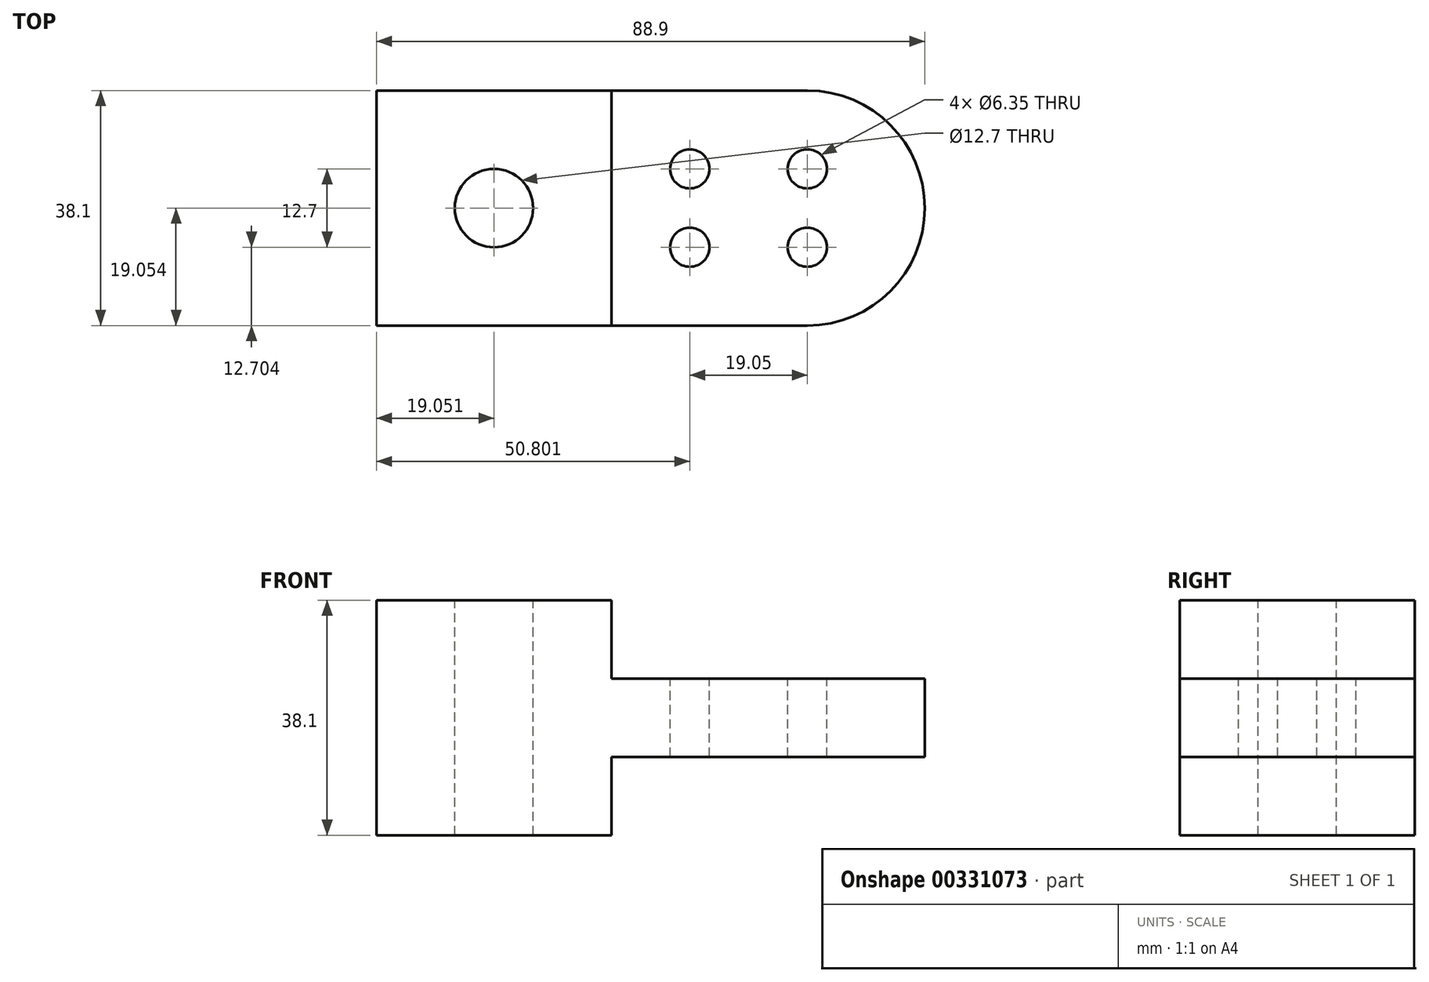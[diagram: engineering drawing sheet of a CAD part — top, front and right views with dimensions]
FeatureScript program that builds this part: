
annotation { "Feature Type Name" : "Feature", "Feature Type Description" : "" }
export const myFeature = defineFeature(function(context is Context, id is Id, definition is map)
    precondition{}
    {
        {
            var Q0;
            Q0=qCreatedBy(makeId("Top.planeOp"),FACE);
            var sketch = newSketch(context, id + "F0", { "sketchPlane" : qUnion([Q0])});
            skLineSegment(sketch, "E0", {"start": v(-35.89, 29.52) * mm, "end": v(2.21, 29.52) * mm});
            skLineSegment(sketch, "E1", {"start": v(2.21, 29.52) * mm, "end": v(2.21, -8.58) * mm});
            skLineSegment(sketch, "E2", {"start": v(2.21, -8.58) * mm, "end": v(-35.89, -8.58) * mm});
            skLineSegment(sketch, "E3", {"start": v(-35.89, -8.58) * mm, "end": v(-35.89, 29.52) * mm});
            skSolve(sketch);
        }
        {
            var Q0;
            Q0 = qSketchRegion(id + "F0", true);
            extrude(context, id + "F1", {"entities" : qUnion([Q0]), "depth" : 38.1 * mm});
        }
        {
            var Q0;
            Q0=makeQuery(id+"F1.opExtrude","SWEPT_FACE",FACE,{"disambiguationData":[OSD([sQuery(id+"F0.wireOp",EDGE,"E2")])]});
            var sketch = newSketch(context, id + "F2", { "sketchPlane" : qUnion([Q0])});
            skLineSegment(sketch, "E4", {"start": v(2.21, 19.05) * mm, "end": v(2.21, 25.4) * mm});
            skLineSegment(sketch, "E5", {"start": v(2.21, 25.4) * mm, "end": v(33.96, 25.4) * mm});
            skLineSegment(sketch, "E6", {"start": v(33.96, 25.4) * mm, "end": v(33.96, 12.7) * mm});
            skLineSegment(sketch, "E7", {"start": v(33.96, 12.7) * mm, "end": v(2.21, 12.7) * mm});
            skLineSegment(sketch, "E8", {"start": v(2.21, 12.7) * mm, "end": v(2.21, 19.05) * mm});
            skSolve(sketch);
        }
        {
            var Q0;
            Q0 = qSketchRegion(id + "F2", true);
            extrude(context, id + "F3", {"entities" : qUnion([Q0]), "operationType" : NewBodyOperationType.ADD, "oppositeDirection" : true, "depth" : 38.1 * mm});
        }
        {
            var Q0;
            Q0=makeQuery(id+"F3.opExtrude","SWEPT_FACE",FACE,{"disambiguationData":[OSD([sQuery(id+"F2.wireOp",EDGE,"E5")])]});
            var sketch = newSketch(context, id + "F4", { "sketchPlane" : qUnion([Q0])});
            skArc(sketch, "E9", {"start": v(33.96, -8.58) * mm, "mid": v(53.01, 10.47) * mm, "end": v(33.96, 29.52) * mm});
            skSolve(sketch);
        }
        {
            var Q0;
            Q0 = qSketchRegion(id + "F4", true);
            var Q1;
            Q1=makeQuery(id+"F4.imprint","IMPRINT",FACE,{"disambiguationData":[TD([[makeQuery(id+"F4.imprint","IMPRINT",EDGE,{"derivedFrom":sQuery(id+"F4.wireOp",EDGE,"E9")}),1.0]])]});
            extrude(context, id + "F5", {"entities" : qUnion([Q0, Q1]), "operationType" : NewBodyOperationType.ADD, "oppositeDirection" : true, "depth" : 12.7 * mm});
        }
        {
            var Q0;
            Q0=makeQuery(id+"F1.opExtrude","CAP_FACE",FACE,{"disambiguationData":[OSD([sQuery(id+"F0.wireOp",EDGE,"E0"),sQuery(id+"F0.wireOp",EDGE,"E1"),sQuery(id+"F0.wireOp",EDGE,"E2"),sQuery(id+"F0.wireOp",EDGE,"E3")])],"isStart":false});
            var sketch = newSketch(context, id + "F6", { "sketchPlane" : qUnion([Q0])});
            skPoint(sketch, "E10", {"position": v(-16.84, 10.47) * mm});
            skPoint(sketch, "E10.positionSnap0", {"position": v(-16.84, 29.52) * mm});
            skPoint(sketch, "E10.positionSnap1", {"position": v(2.21, 10.47) * mm});
            skSolve(sketch);
        }
        {
            var Q0;
            {var subQ0=sQuery(id+"F2.wireOp",EDGE,"E5");Q0=makeQuery(id+"F5.boolean.opBoolean","MERGE",FACE,{"derivedFrom":[makeQuery(id+"F3.opExtrude","SWEPT_FACE",FACE,{"disambiguationData":[OSD([subQ0])]}),makeQuery(id+"F5.opExtrude","CAP_FACE",FACE,{"disambiguationData":[OSD([subQ0,sQuery(id+"F2.wireOp",EDGE,"E6"),sQuery(id+"F4.wireOp",EDGE,"E9")])],"isStart":true})]});}
            var sketch = newSketch(context, id + "F7", { "sketchPlane" : qUnion([Q0])});
            skPoint(sketch, "E11", {"position": v(14.91, 16.82) * mm});
            skPoint(sketch, "E12", {"position": v(14.91, 4.12) * mm});
            skPoint(sketch, "E13", {"position": v(33.96, 4.12) * mm});
            skPoint(sketch, "E14", {"position": v(33.96, 16.82) * mm});
            skSolve(sketch);
        }
        {
            var Q0;
            Q0=sQuery(id+"F6.wireOp",VERTEX,"E10");
            var Q1;
            Q1=makeQuery(id+"F1.opExtrude","SWEPT_BODY",BODY,{"disambiguationData":[OSD([sQuery(id+"F0.wireOp",EDGE,"E0"),sQuery(id+"F0.wireOp",EDGE,"E1"),sQuery(id+"F0.wireOp",EDGE,"E2"),sQuery(id+"F0.wireOp",EDGE,"E3")])]});
            hole(context, id + "F8", {"style" : HoleStyle.SIMPLE, "endStyle" : HoleEndStyle.THROUGH, "holeDiameter" : 12.7 * mm, "tappedDepth" : 12.7 * mm, "tapClearance" : 3, "locations" : qUnion([Q0]), "scope" : qUnion([Q1])});
        }
        {
            var Q0;
            Q0=sQuery(id+"F7.wireOp",VERTEX,"E11");
            var Q1;
            Q1=sQuery(id+"F7.wireOp",VERTEX,"E12");
            var Q2;
            Q2=sQuery(id+"F7.wireOp",VERTEX,"E13");
            var Q3;
            Q3=sQuery(id+"F7.wireOp",VERTEX,"E14");
            var Q4;
            Q4=makeQuery(id+"F1.opExtrude","SWEPT_BODY",BODY,{"disambiguationData":[OSD([sQuery(id+"F0.wireOp",EDGE,"E0"),sQuery(id+"F0.wireOp",EDGE,"E1"),sQuery(id+"F0.wireOp",EDGE,"E2"),sQuery(id+"F0.wireOp",EDGE,"E3")])]});
            hole(context, id + "F9", {"style" : HoleStyle.SIMPLE, "endStyle" : HoleEndStyle.THROUGH, "holeDiameter" : 6.35 * mm, "tappedDepth" : 12.7 * mm, "tapClearance" : 3, "locations" : qUnion([Q0, Q1, Q2, Q3]), "scope" : qUnion([Q4])});
        }
    });
